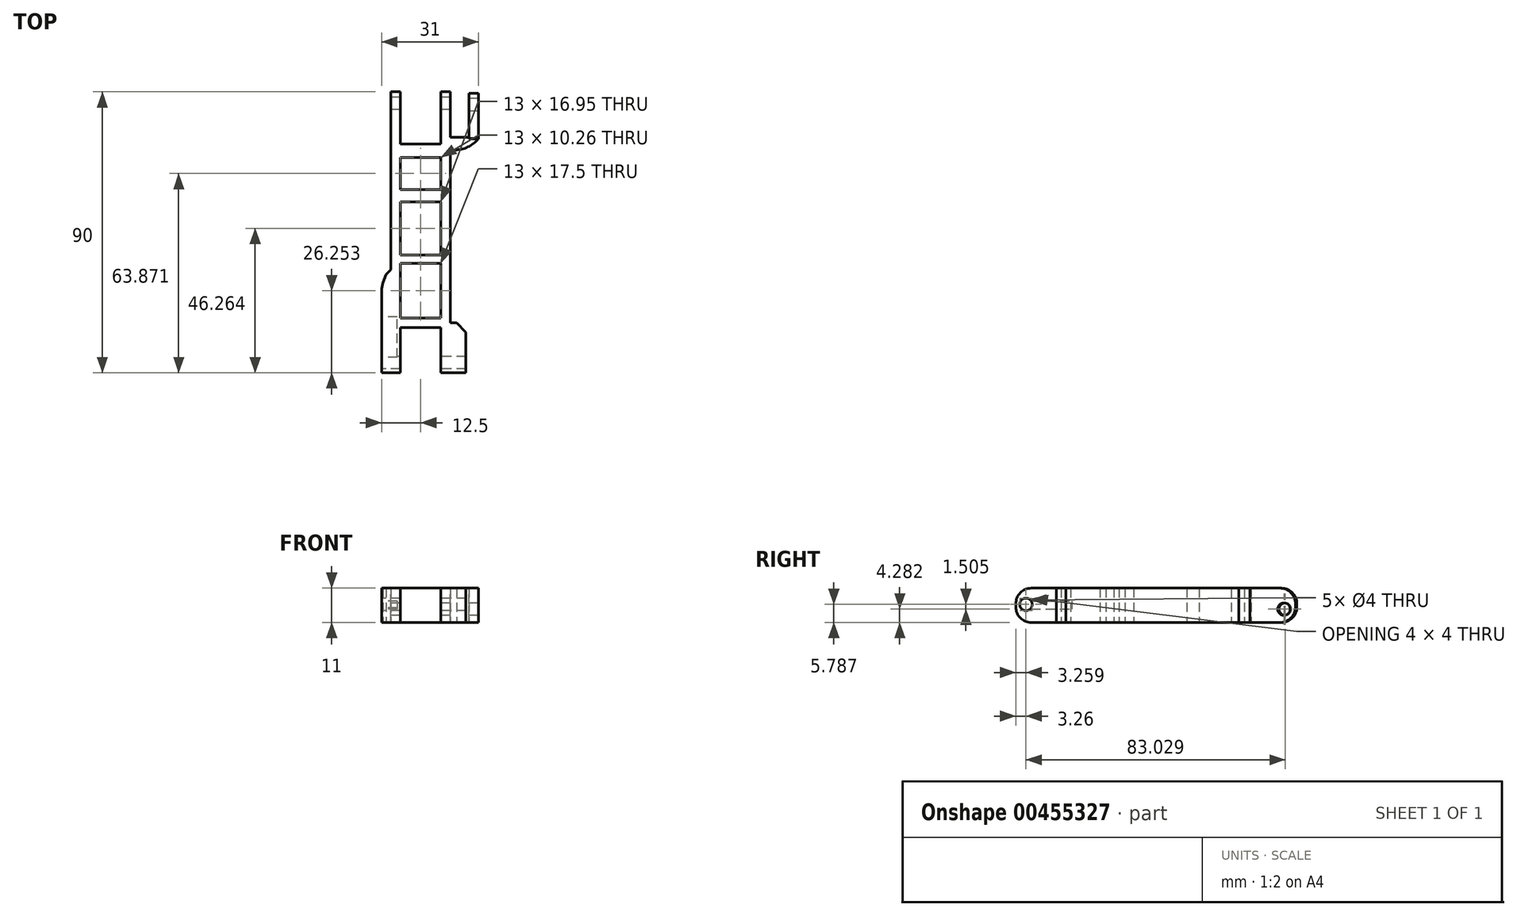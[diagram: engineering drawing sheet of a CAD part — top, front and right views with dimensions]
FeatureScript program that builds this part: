
annotation { "Feature Type Name" : "Feature", "Feature Type Description" : "" }
export const myFeature = defineFeature(function(context is Context, id is Id, definition is map)
    precondition{}
    {
        {
            var Q0;
            Q0=qCreatedBy(makeId("Top.planeOp"),FACE);
            var sketch = newSketch(context, id + "F0", { "sketchPlane" : qUnion([Q0])});
            skLineSegment(sketch, "E0.bottom", {"start": v(4.22, 58.58) * mm, "end": v(7.22, 58.58) * mm});
            skLineSegment(sketch, "E0.top", {"start": v(4.22, -31.42) * mm, "end": v(7.22, -31.42) * mm});
            skLineSegment(sketch, "E0.left", {"start": v(4.22, 58.58) * mm, "end": v(4.22, -31.42) * mm});
            skLineSegment(sketch, "E0.right", {"start": v(7.22, 58.58) * mm, "end": v(7.22, -31.42) * mm});
            skLineSegment(sketch, "E1.bottom", {"start": v(7.22, -15.42) * mm, "end": v(12.22, -15.42) * mm});
            skLineSegment(sketch, "E1.top", {"start": v(7.22, -31.42) * mm, "end": v(12.22, -31.42) * mm});
            skLineSegment(sketch, "E1.left", {"start": v(7.22, -15.42) * mm, "end": v(7.22, -31.42) * mm});
            skLineSegment(sketch, "E1.right", {"start": v(12.22, -15.42) * mm, "end": v(12.22, -31.42) * mm});
            skLineSegment(sketch, "E2.bottom", {"start": v(-8.78, 58.58) * mm, "end": v(-11.78, 58.58) * mm});
            skLineSegment(sketch, "E2.top", {"start": v(-8.78, 3.58) * mm, "end": v(-11.78, 3.58) * mm});
            skLineSegment(sketch, "E2.left", {"start": v(-8.78, 58.58) * mm, "end": v(-8.78, 3.58) * mm});
            skLineSegment(sketch, "E2.right", {"start": v(-11.78, 58.58) * mm, "end": v(-11.78, 3.58) * mm});
            skLineSegment(sketch, "E3.bottom", {"start": v(-8.78, 37.58) * mm, "end": v(4.22, 37.58) * mm});
            skLineSegment(sketch, "E3.top", {"start": v(-8.78, 41.81) * mm, "end": v(4.22, 41.81) * mm});
            skLineSegment(sketch, "E3.left", {"start": v(-8.78, 41.81) * mm, "end": v(-8.78, 37.58) * mm});
            skLineSegment(sketch, "E3.right", {"start": v(4.22, 41.81) * mm, "end": v(4.22, 37.58) * mm});
            skLineSegment(sketch, "E4.bottom", {"start": v(-8.78, 27.32) * mm, "end": v(4.22, 27.32) * mm});
            skLineSegment(sketch, "E4.top", {"start": v(-8.78, 23.32) * mm, "end": v(4.22, 23.32) * mm});
            skLineSegment(sketch, "E4.left", {"start": v(-8.78, 27.32) * mm, "end": v(-8.78, 23.32) * mm});
            skLineSegment(sketch, "E4.right", {"start": v(4.22, 27.32) * mm, "end": v(4.22, 23.32) * mm});
            skLineSegment(sketch, "E5.bottom", {"start": v(-8.78, 3.58) * mm, "end": v(4.22, 3.58) * mm});
            skLineSegment(sketch, "E5.top", {"start": v(-8.78, 6.37) * mm, "end": v(4.22, 6.37) * mm});
            skLineSegment(sketch, "E5.left", {"start": v(-8.78, 3.58) * mm, "end": v(-8.78, 6.37) * mm});
            skLineSegment(sketch, "E5.right", {"start": v(4.22, 3.58) * mm, "end": v(4.22, 6.37) * mm});
            skLineSegment(sketch, "E6.bottom", {"start": v(-8.78, 3.58) * mm, "end": v(-14.78, 3.58) * mm});
            skLineSegment(sketch, "E6.top", {"start": v(-8.78, -31.42) * mm, "end": v(-14.78, -31.42) * mm});
            skLineSegment(sketch, "E6.left", {"start": v(-8.78, 3.58) * mm, "end": v(-8.78, -31.42) * mm});
            skLineSegment(sketch, "E6.right", {"start": v(-14.78, 3.58) * mm, "end": v(-14.78, -31.42) * mm});
            skLineSegment(sketch, "E7.bottom", {"start": v(-8.78, -13.92) * mm, "end": v(4.22, -13.92) * mm});
            skLineSegment(sketch, "E7.top", {"start": v(-8.78, -16.92) * mm, "end": v(4.22, -16.92) * mm});
            skLineSegment(sketch, "E7.left", {"start": v(-8.78, -13.92) * mm, "end": v(-8.78, -16.92) * mm});
            skLineSegment(sketch, "E7.right", {"start": v(4.22, -13.92) * mm, "end": v(4.22, -16.92) * mm});
            skLineSegment(sketch, "E8.bottom", {"start": v(-8.78, -16.92) * mm, "end": v(-5.78, -16.92) * mm});
            skLineSegment(sketch, "E8.top", {"start": v(-8.78, -30.92) * mm, "end": v(-5.78, -30.92) * mm});
            skLineSegment(sketch, "E8.left", {"start": v(-8.78, -16.92) * mm, "end": v(-8.78, -30.92) * mm});
            skLineSegment(sketch, "E8.right", {"start": v(-5.78, -16.92) * mm, "end": v(-5.78, -30.92) * mm});
            skLineSegment(sketch, "E9.bottom", {"start": v(13.22, 58.58) * mm, "end": v(16.22, 58.58) * mm});
            skLineSegment(sketch, "E9.top", {"start": v(13.22, 43.58) * mm, "end": v(16.22, 43.58) * mm});
            skLineSegment(sketch, "E9.left", {"start": v(13.22, 58.58) * mm, "end": v(13.22, 43.58) * mm});
            skLineSegment(sketch, "E9.right", {"start": v(16.22, 58.58) * mm, "end": v(16.22, 43.58) * mm});
            skLineSegment(sketch, "E10.bottom", {"start": v(7.22, 43.96) * mm, "end": v(16.22, 43.96) * mm});
            skLineSegment(sketch, "E10.top", {"start": v(7.22, 39.96) * mm, "end": v(16.22, 39.96) * mm});
            skLineSegment(sketch, "E10.left", {"start": v(7.22, 43.96) * mm, "end": v(7.22, 39.96) * mm});
            skLineSegment(sketch, "E10.right", {"start": v(16.22, 43.96) * mm, "end": v(16.22, 39.96) * mm});
            skSolve(sketch);
        }
        {
            var Q0;
            {var subQ4=sQuery(id+"F0.wireOp",EDGE,"E2.bottom");Q0=makeQuery(id+"F0.imprint","IMPRINT",FACE,{"disambiguationData":[TD([[makeQuery(id+"F0.imprint","IMPRINT",EDGE,{"derivedFrom":subQ4}),1.0]])]});}
            var Q1;
            {var subQ4=sQuery(id+"F0.wireOp",EDGE,"E6.top");Q1=makeQuery(id+"F0.imprint","IMPRINT",FACE,{"disambiguationData":[TD([[makeQuery(id+"F0.imprint","IMPRINT",EDGE,{"derivedFrom":subQ4}),-1.0]])]});}
            var Q2;
            Q2=makeQuery(id+"F0.imprint","IMPRINT",FACE,{"disambiguationData":[TD([[makeQuery(id+"F0.imprint","IMPRINT",EDGE,{"derivedFrom":sQuery(id+"F0.wireOp",EDGE,"E7.bottom")}),-1.0]])]});
            var Q3;
            Q3=makeQuery(id+"F0.imprint","IMPRINT",FACE,{"disambiguationData":[TD([[makeQuery(id+"F0.imprint","IMPRINT",EDGE,{"derivedFrom":sQuery(id+"F0.wireOp",EDGE,"E8.bottom")}),-1.0]])]});
            var Q4;
            {var subQ3=sQuery(id+"F0.wireOp",EDGE,"E0.bottom");Q4=makeQuery(id+"F0.imprint","IMPRINT",FACE,{"disambiguationData":[TD([[makeQuery(id+"F0.imprint","IMPRINT",EDGE,{"derivedFrom":subQ3}),-1.0]])]});}
            var Q5;
            Q5=makeQuery(id+"F0.imprint","IMPRINT",FACE,{"disambiguationData":[TD([[makeQuery(id+"F0.imprint","IMPRINT",EDGE,{"derivedFrom":sQuery(id+"F0.wireOp",EDGE,"E1.bottom")}),-1.0]])]});
            var Q6;
            Q6=makeQuery(id+"F0.imprint","IMPRINT",FACE,{"disambiguationData":[TD([[makeQuery(id+"F0.imprint","IMPRINT",EDGE,{"derivedFrom":sQuery(id+"F0.wireOp",EDGE,"E5.bottom")}),1.0]])]});
            var Q7;
            Q7=makeQuery(id+"F0.imprint","IMPRINT",FACE,{"disambiguationData":[TD([[makeQuery(id+"F0.imprint","IMPRINT",EDGE,{"derivedFrom":sQuery(id+"F0.wireOp",EDGE,"E4.bottom")}),-1.0]])]});
            var Q8;
            Q8=makeQuery(id+"F0.imprint","IMPRINT",FACE,{"disambiguationData":[TD([[makeQuery(id+"F0.imprint","IMPRINT",EDGE,{"derivedFrom":sQuery(id+"F0.wireOp",EDGE,"E3.bottom")}),1.0]])]});
            var Q9;
            {var subQ0=sQuery(id+"F0.wireOp",EDGE,"E9.bottom");Q9=makeQuery(id+"F0.imprint","IMPRINT",FACE,{"disambiguationData":[TD([[makeQuery(id+"F0.imprint","IMPRINT",EDGE,{"derivedFrom":subQ0}),-1.0]])]});}
            var Q10;
            {var subQ5=sQuery(id+"F0.wireOp",EDGE,"E9.top");Q10=makeQuery(id+"F0.imprint","IMPRINT",FACE,{"disambiguationData":[TD([[makeQuery(id+"F0.imprint","IMPRINT",EDGE,{"derivedFrom":subQ5}),-1.0]])]});}
            extrude(context, id + "F1", {"entities" : qUnion([Q0, Q1, Q2, Q3, Q4, Q5, Q6, Q7, Q8, Q9, Q10]), "depth" : 11 * mm});
        }
        {
            var Q0;
            Q0=makeQuery(id+"F1.opExtrude","SWEPT_EDGE",EDGE,{"disambiguationData":[OSD([sQuery(id+"F0.wireOp",EDGE,"E10.top"),sQuery(id+"F0.wireOp",EDGE,"E10.right")])]});
            fillet(context, id + "F2", {"entities" : qUnion([Q0]), "radius" : 9.66 * mm, "tangentPropagation" : true, "allowEdgeOverflow" : false});
        }
        {
            var Q0;
            Q0=makeQuery(id+"F1.opExtrude","SWEPT_FACE",FACE,{"disambiguationData":[OSD([sQuery(id+"F0.wireOp",EDGE,"E2.right")])]});
            var sketch = newSketch(context, id + "F3", { "sketchPlane" : qUnion([Q0])});
            skCircle(sketch, "E11", {"center": v(-54.87, 4.28) * mm, "radius": 2 * mm});
            skSolve(sketch);
        }
        {
            var Q0;
            Q0=makeQuery(id+"F1.opExtrude","SWEPT_EDGE",EDGE,{"disambiguationData":[OSD([sQuery(id+"F0.wireOp",EDGE,"E6.bottom"),sQuery(id+"F0.wireOp",EDGE,"E6.right")])]});
            chamfer(context, id + "F4", {"entities" : qUnion([Q0]), "width" : 5 * mm, "tangentPropagation" : true});
        }
        {
            var Q0;
            {var subQ0=sQuery(id+"F0.wireOp",EDGE,"E6.right");Q0=makeQuery(id+"F4.opChamfer","BLEND_EDGE",EDGE,{"blendedFrom":[makeQuery(id+"F1.opExtrude","SWEPT_EDGE",EDGE,{"disambiguationData":[OSD([sQuery(id+"F0.wireOp",EDGE,"E6.bottom"),subQ0])]}),makeQuery(id+"F1.opExtrude","SWEPT_FACE",FACE,{"disambiguationData":[OSD([subQ0])]})],"blendedInto":[makeQuery(id+"F1.opExtrude","SWEPT_FACE",FACE,{"disambiguationData":[OSD([subQ0])]})]});}
            chamfer(context, id + "F5", {"entities" : qUnion([Q0]), "width" : 5 * mm, "tangentPropagation" : true});
        }
        {
            var Q0;
            {var subQ0=sQuery(id+"F0.wireOp",EDGE,"E6.right");var subQ1=makeQuery(id+"F1.opExtrude","SWEPT_FACE",FACE,{"disambiguationData":[OSD([subQ0])]});Q0=makeQuery(id+"F5.opChamfer","BLEND_EDGE",EDGE,{"blendedFrom":[makeQuery(id+"F4.opChamfer","BLEND_EDGE",EDGE,{"blendedFrom":[makeQuery(id+"F1.opExtrude","SWEPT_EDGE",EDGE,{"disambiguationData":[OSD([sQuery(id+"F0.wireOp",EDGE,"E6.bottom"),subQ0])]}),subQ1],"blendedInto":[subQ1]}),subQ1],"blendedInto":[subQ1]});}
            chamfer(context, id + "F6", {"entities" : qUnion([Q0]), "width" : 5 * mm, "tangentPropagation" : true});
        }
        {
            var Q0;
            Q0=makeQuery(id+"F1.opExtrude","CAP_EDGE",EDGE,{"disambiguationData":[OSD([sQuery(id+"F0.wireOp",EDGE,"E0.top"),sQuery(id+"F0.wireOp",EDGE,"E1.top")])],"isStart":true});
            var Q1;
            Q1=makeQuery(id+"F1.opExtrude","CAP_EDGE",EDGE,{"disambiguationData":[OSD([sQuery(id+"F0.wireOp",EDGE,"E0.top"),sQuery(id+"F0.wireOp",EDGE,"E1.top")])],"isStart":false});
            var Q2;
            Q2=makeQuery(id+"F1.opExtrude","CAP_EDGE",EDGE,{"disambiguationData":[OSD([sQuery(id+"F0.wireOp",EDGE,"E6.top")])],"isStart":true});
            var Q3;
            Q3=makeQuery(id+"F1.opExtrude","CAP_EDGE",EDGE,{"disambiguationData":[OSD([sQuery(id+"F0.wireOp",EDGE,"E6.top")])],"isStart":false});
            fillet(context, id + "F7", {"entities" : qUnion([Q0, Q1, Q2, Q3]), "radius" : 5 * mm, "tangentPropagation" : true, "allowEdgeOverflow" : false});
        }
        {
            var Q0;
            Q0=makeQuery(id+"F1.opExtrude","CAP_EDGE",EDGE,{"disambiguationData":[OSD([sQuery(id+"F0.wireOp",EDGE,"E9.bottom")])],"isStart":true});
            var Q1;
            Q1=makeQuery(id+"F1.opExtrude","CAP_EDGE",EDGE,{"disambiguationData":[OSD([sQuery(id+"F0.wireOp",EDGE,"E9.bottom")])],"isStart":false});
            var Q2;
            Q2=makeQuery(id+"F1.opExtrude","CAP_EDGE",EDGE,{"disambiguationData":[OSD([sQuery(id+"F0.wireOp",EDGE,"E0.bottom")])],"isStart":false});
            var Q3;
            Q3=makeQuery(id+"F1.opExtrude","CAP_EDGE",EDGE,{"disambiguationData":[OSD([sQuery(id+"F0.wireOp",EDGE,"E0.bottom")])],"isStart":true});
            var Q4;
            Q4=makeQuery(id+"F1.opExtrude","CAP_EDGE",EDGE,{"disambiguationData":[OSD([sQuery(id+"F0.wireOp",EDGE,"E2.bottom")])],"isStart":false});
            var Q5;
            Q5=makeQuery(id+"F1.opExtrude","CAP_EDGE",EDGE,{"disambiguationData":[OSD([sQuery(id+"F0.wireOp",EDGE,"E2.bottom")])],"isStart":true});
            fillet(context, id + "F8", {"entities" : qUnion([Q0, Q1, Q2, Q3, Q4, Q5]), "radius" : 5 * mm, "tangentPropagation" : true, "allowEdgeOverflow" : false});
        }
        {
            var Q0;
            Q0=makeQuery(id+"F1.opExtrude","SWEPT_EDGE",EDGE,{"disambiguationData":[OSD([sQuery(id+"F0.wireOp",EDGE,"E1.bottom"),sQuery(id+"F0.wireOp",EDGE,"E1.right")])]});
            chamfer(context, id + "F9", {"entities" : qUnion([Q0]), "width" : 3 * mm, "tangentPropagation" : true});
        }
        {
            var Q0;
            Q0=makeQuery(id+"F3.imprint","IMPRINT",FACE,{"disambiguationData":[TD([[makeQuery(id+"F3.imprint","IMPRINT",EDGE,{"derivedFrom":sQuery(id+"F3.wireOp",EDGE,"E11")}),-1.0]])]});
            var sketch = newSketch(context, id + "F10", { "sketchPlane" : qUnion([Q0])});
            skSolve(sketch);
        }
        {
            var Q0;
            Q0 = qSketchRegion(id + "F10", true);
            var Q1;
            Q1=makeQuery(id+"F3.imprint","IMPRINT",FACE,{"disambiguationData":[TD([[makeQuery(id+"F3.imprint","IMPRINT",EDGE,{"derivedFrom":sQuery(id+"F3.wireOp",EDGE,"E11")}),1.0]])]});
            extrude(context, id + "F11", {"entities" : qUnion([Q0, Q1]), "operationType" : NewBodyOperationType.REMOVE, "oppositeDirection" : true, "depth" : 29.9 * mm});
        }
        {
            var Q0;
            Q0=makeQuery(id+"F1.opExtrude","SWEPT_BODY",BODY,{"disambiguationData":[OSD([sQuery(id+"F0.wireOp",EDGE,"E9.bottom"),sQuery(id+"F0.wireOp",EDGE,"E9.left"),sQuery(id+"F0.wireOp",EDGE,"E9.right"),sQuery(id+"F0.wireOp",EDGE,"E10.bottom")])]});
            transform(context, id + "F12", {"entities" : qUnion([Q0]), "transformType" : TransformType.TRANSLATION_3D, "dx" : 0 * mm, "dy" : -0.43 * mm, "dz" : 0 * mm, "makeCopy" : false});
        }
        {
            var Q0;
            Q0=makeQuery(id+"F1.opExtrude","SWEPT_FACE",FACE,{"disambiguationData":[OSD([sQuery(id+"F0.wireOp",EDGE,"E6.right")])]});
            var sketch = newSketch(context, id + "F13", { "sketchPlane" : qUnion([Q0])});
            skCircle(sketch, "E12", {"center": v(28.16, 5.79) * mm, "radius": 2 * mm});
            skSolve(sketch);
        }
        {
            var Q0;
            Q0 = qSketchRegion(id + "F13", true);
            var Q1;
            Q1=makeQuery(id+"F13.imprint","IMPRINT",FACE,{"disambiguationData":[TD([[makeQuery(id+"F13.imprint","IMPRINT",EDGE,{"derivedFrom":sQuery(id+"F13.wireOp",EDGE,"E12")}),1.0]])]});
            extrude(context, id + "F14", {"entities" : qUnion([Q0, Q1]), "operationType" : NewBodyOperationType.REMOVE, "oppositeDirection" : true, "depth" : 37.6 * mm});
        }
        {
            var Q0;
            Q0=makeQuery(id+"F1.opExtrude","SWEPT_FACE",FACE,{"disambiguationData":[OSD([sQuery(id+"F0.wireOp",EDGE,"E6.right")])]});
            var sketch = newSketch(context, id + "F15", { "sketchPlane" : qUnion([Q0])});
            skLineSegment(sketch, "E13.bottom", {"start": v(26.5, 6.9) * mm, "end": v(13.5, 6.9) * mm});
            skLineSegment(sketch, "E13.top", {"start": v(26.5, 4.28) * mm, "end": v(13.5, 4.28) * mm});
            skLineSegment(sketch, "E13.left", {"start": v(26.5, 6.9) * mm, "end": v(26.5, 4.28) * mm});
            skLineSegment(sketch, "E13.right", {"start": v(13.5, 6.9) * mm, "end": v(13.5, 4.28) * mm});
            skSolve(sketch);
        }
        {
            var Q0;
            {var subQ4=sQuery(id+"F15.wireOp",EDGE,"E13.bottom");Q0=makeQuery(id+"F15.imprint","IMPRINT",FACE,{"disambiguationData":[TD([[makeQuery(id+"F15.imprint","IMPRINT",EDGE,{"derivedFrom":subQ4}),1.0]])]});}
            extrude(context, id + "F16", {"entities" : qUnion([Q0]), "operationType" : NewBodyOperationType.REMOVE, "oppositeDirection" : true, "depth" : 5 * mm});
        }
    });
